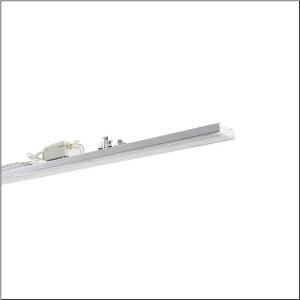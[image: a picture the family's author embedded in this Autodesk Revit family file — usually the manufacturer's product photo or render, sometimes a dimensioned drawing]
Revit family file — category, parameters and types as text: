
# Revit family: licross_r__21_recessed_mo_52tl19cn485g_b288
name_source: partatom
category: Lighting Fixtures
units: mm (PartAtom-declared; Revit-internal decimal feet)

## family parameters
Cut with Voids When Loaded = No
Host = Face
Light Source = No
Part Type = Normal
Room Calculation Point = No
Round Connector Dimension = Use Diameter
Shared = No

## types (1)
- --- (1 x LED, 8870 lm, 49.9 W, 4000K)
    Apparent Load = 50 VA
    CIE Flux Codes = 55 90 98 100 100
    Color Rendering = 80
    Color Temperature = 4000K
    Default Elevation = 1800 mm
    Description = Licross® 21 Recessed MO, luminaire insert, of sheet steel, galvanised, coil coated, white, length: 1.500mm, width: 66mm, height: 67mm, LED rated luminous flux: 8.880lm, light colour: 840, control gear: ON/OFF Multilumen, CLOi, control gear: ECG DALI, with plug, 5-pole, with phase selection, mains connection: 220..240V, AC, 50/60Hz, start of lifetime: 50W, end of service life: 61W, halogen-free wiring, primary light control with lens, of plastic, primary optical cover: cover, of PMMA, light emission: direct distribution, primary light characteristic: double asymmetric, protection rating (complete): IP40, insulation class (complete): insulation class I (protective earthing), certification: CE, ENEC, VDE, UKCA, protection symbol: D if used in an environment without relevant dust loads with corresponding accessories, impact resistance: IK06, permissible ambient temperature for indoor applications: -35..+40°C, corresponds to IFS (International Featured Standards) requirements for safety and quality in the food industry, reducing of maximum allowable ambient temperature of 5°C with ceiling mounting, LABS conformity tested according to VDMA 24364:2018-05, packaging unit: 1 piece
    Height = 58 mm
    Lamp = 1 x LED
    Lamp Light Flux = 8870 lm
    Lamp Power = 49.9 W
    Lamp count = 1
    Length = 1500 mm
    Luminous efficacy = 178 lm/W
    Manufacturer = Siteco
    ModVariant = No
    Model = 52TL19CN485G
    Mounting Place = Ceiling
    Mounting Type = Pendant
    Number of Poles = 1
    OnlyDefault = Yes
    Power Factor = 1
    Product Name = Licross® 21 Recessed MO
    Product group = luminaire insert
    ProductGroupID = 901
    Protection Class = Protection class I
    Protection Degree = IP 40
    RLX_Detail_Level = 1
    RLX_Emergency_Light_Flux = 0 lm
    RLX_Emergency_Type = 0
    RLX_Emergency_Type_DB = No
    RlxData = <blob elided: 22349 chars, md5=b51cfea7>
    Socket = socket
    Standby Power = 0 W
    System Light Flux = 8870 lm
    System Power = 50 W
    Type Comments = factory setting: luminous flux: 100 % | (A | C | E) | 116 mA
    Type Image = l_1296930.jpg
    URL = http://relux.com
    VarID = @adj_040897
    Voltage = 0 V
    Weight = 0.00 kg
    Width = 66 mm

## geometry (parser evidence)
native form markers: Blend x4, Sweep x10
no freeform markers — native parametric forms only
